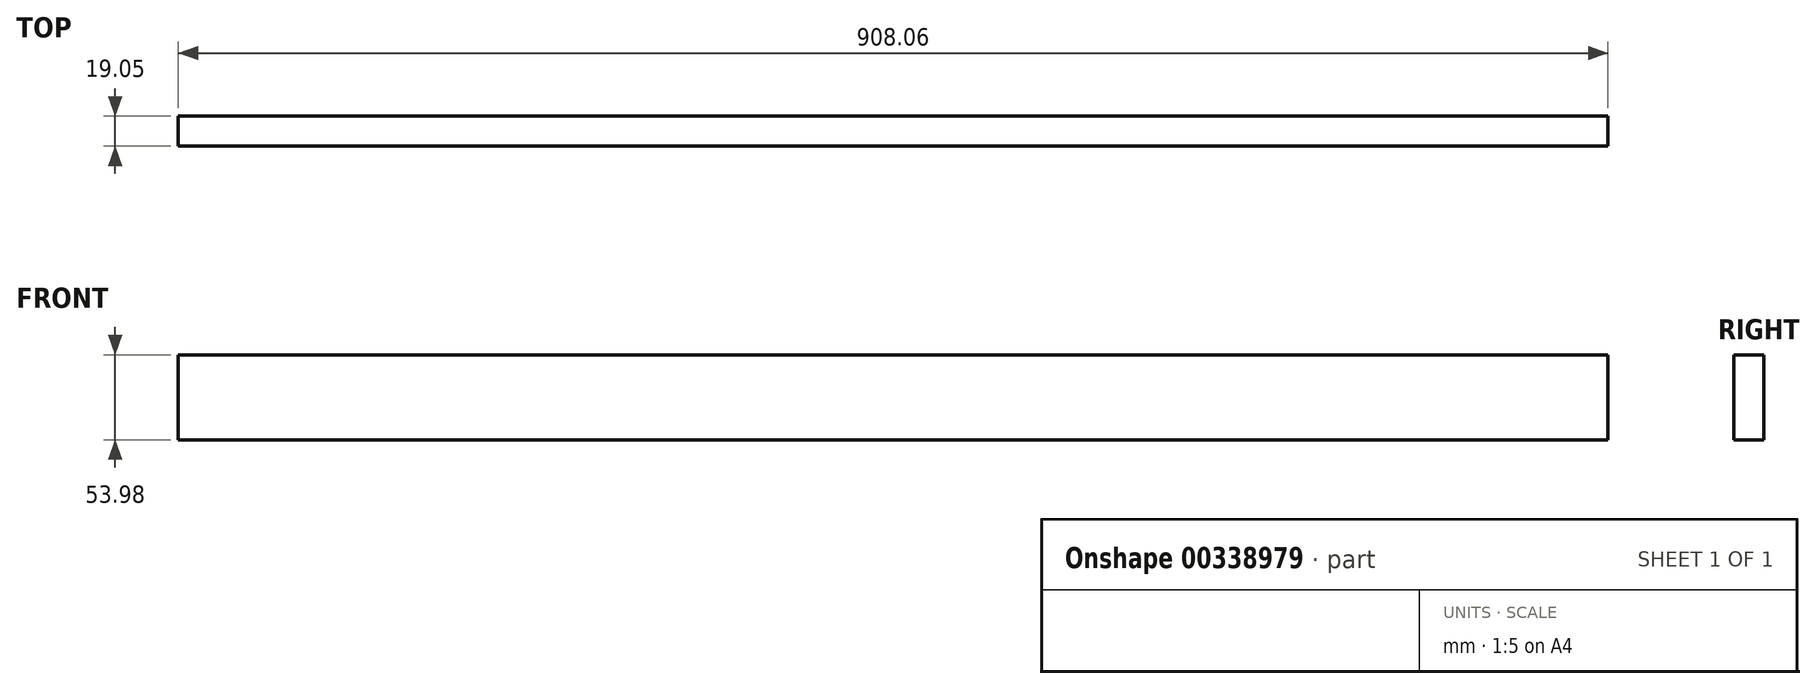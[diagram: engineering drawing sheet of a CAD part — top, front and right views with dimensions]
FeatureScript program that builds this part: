
annotation { "Feature Type Name" : "Feature", "Feature Type Description" : "" }
export const myFeature = defineFeature(function(context is Context, id is Id, definition is map)
    precondition{}
    {
        {
            var Q0;
            Q0=qCreatedBy(makeId("Front.planeOp"),FACE);
            var sketch = newSketch(context, id + "F0", { "sketchPlane" : qUnion([Q0])});
            skLineSegment(sketch, "E0.bottom", {"start": v(454.03, -26.99) * mm, "end": v(-454.03, -26.99) * mm});
            skLineSegment(sketch, "E0.top", {"start": v(454.03, 26.99) * mm, "end": v(-454.03, 26.99) * mm});
            skLineSegment(sketch, "E0.left", {"start": v(454.03, -26.99) * mm, "end": v(454.03, 26.99) * mm});
            skLineSegment(sketch, "E0.right", {"start": v(-454.03, -26.99) * mm, "end": v(-454.03, 26.99) * mm});
            skPoint(sketch, "E0.middle", {"position": v(0, 0) * mm});
            skSolve(sketch);
        }
        {
            var Q0;
            Q0 = qSketchRegion(id + "F0", true);
            extrude(context, id + "F1", {"entities" : qUnion([Q0]), "depth" : 19.05 * mm});
        }
    });
